# Revit family: Führungsklammer mit Abheb. mit Gleitunt., Typ 2A (I-III)
name_source: partatom
category: HLS-Bauteile
units: mm (PartAtom-declared; Revit-internal decimal feet)

## family parameters
Arbeitsebenenbasiert = Ja
Beim Laden mit Abzugskörper schneiden = Nein
Bemaßung runder Anschluss = Durchmesser verwenden
Beschriftungsausrichtung beibehalten = Nein
Gemeinsam genutzt = Ja
Immer vertikal = Nein
Raumberechnungspunkt = Nein
Teiletyp = Normal

## types (3) — shared parameters
Anzahl PE-Gleitunterlagen = 2
Fabrikat = MEFA
Firma = MEFA Befestigungs- und Montagesysteme GmbH
Gleitreibungsfaktor = 0,2
Haftreibungsfaktor = 0,15
Material = Stahl
Materialname = S235
Mengeneinheit = Set
Oberflaeche = feuerstückverzinkt
Sicherheitsfaktor = 1.54
Typ = mit Abhebesicherung
Vorgabe-Ansicht = 1219 mm
max. Stärke Gleitplatte = 12 mm  [stored 0.0393701 ft]
max. Temperaturbeständigkeit = 80 °C
max. zul. Last Zug = 3.50 kN
max. zul. Schublast = 4.00 kN
vpe = 1

## per-type parameters (varying)
| type | Artikelnummer | EAN | Faktor1 | Gewicht | Gewicht pro Bauteil | Gewindestangentyp | Klemmweite | Klemmweite Flansch max. | Klemmweite Flansch min. | Kurztext1 | Kurztext2 | Länge Gewindestange M12 | für Träger HEA | für Träger HEB | für Träger IPE | min. Klemmdicke |
| Führungsklammer Set Typ 2A mit Abheb. mit Gleitunt., Typ 2A III | 14710006 | 4250928432490 | 115 mm  [stored 0.377297 ft] | 2.19 kg | 2.19 kg | M12 x 310 | HEA 200, HEB180-200, IPE360-400, | 200 mm  [stored 0.656168 ft] | 170 mm  [stored 0.557743 ft] | Führungsklammer Typ 2A III | für HEA 200 HEB 180-200 | 310 mm  [stored 1.01706 ft] | 200 | 180-200 |  | 10 mm |
| Führungsklammer Set Typ 2A mit Abheb. mit Gleitunt., Typ 2A II | 14710005 | 4250928432483 | 85 mm  [stored 0.278871 ft] | 2.13 kg | 2.13 kg | M12 x 270 | HEA160-180, HEB140-160, IPE270-330, IPEa300-360, IPEo270-330 | 180 mm  [stored 0.590551 ft] | 160 mm  [stored 0.524934 ft] | Führungsklammer Typ 2A II | für HEA 160-180 HEB 140-160 IPE 270-330 | 270 mm  [stored 0.885827 ft] | 160-180 | 140-160 | 270-330 | 9 mm |
| Führungsklammer Set Typ 2A mit Abheb. mit Gleitunt., Typ 2A I | 14710004 | 4250928432476 | 5 mm  [stored 0.0164042 ft] | 2.06 kg | 2.06 kg | M12 x 220 | HEA 100-140, HEB100-120, IPE200-240, IPEa240-270, IPEo200-240 | 140 mm  [stored 0.459318 ft] | 100 mm  [stored 0.328084 ft] | Führungsklammer Typ 2A I | für HEA 100-140 HEB 100-120 IPE 200-240 | 220 mm  [stored 0.721785 ft] | 100-140 | 100-120 | 200-240 | 5.2 mm |

note: [stored X ft] marks values corroborated as IEEE doubles in the binary element streams (Revit-internal decimal feet)

## geometry (parser evidence)
native form markers: Sweep x1
no freeform markers — native parametric forms only
